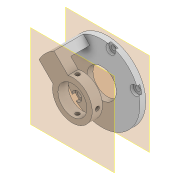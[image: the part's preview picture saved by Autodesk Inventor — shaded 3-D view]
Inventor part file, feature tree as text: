
AUTODESK INVENTOR PART (.ipt)
format: ipt  version: 2022 (Build 260153000, 153)  size: 205,824 bytes
history: native  units: in
note: dims shown in document units (in); Inventor stores cm internally (conversion verified against a paired STEP export)
features: sketch x5, reference x5, extrude x4, other x4, plane x2, hole x1, pattern_circular x1, projected_geometry x1
ambient origin geometry x8: Origin, YZ Plane, XZ Plane, XY Plane, X Axis, Y Axis, Z Axis, Center Point
bodies: Solid1 (feature_tree)
feature tree (23):
  plane  "Work Plane1"
  extrude  "Extrusion1"  Depth=0.7874in
  hole  "Bohrung1"  [1 undecoded]
  plane  "Arbeitsebene3"
  extrude  "Extrusion13"  TaperAngle=135.0deg  [1 undecoded]
  extrude  "Extrusion14"  Depth=0.3937in
  extrude  "Extrusion15"  Depth=0.3937in
  pattern_circular  "Runde Anordnung1"  [2 undecoded]
  sketch  "Sketch1"  dims[d0=0.1575in d1=0.0in]
  reference  "Reference1"
  reference  "Reference5"
  reference  "Reference6"
  reference  "Reference7"
  sketch  "Skizze4"  dims[d9=0.126in d10=0.75in d11=0.2559in d12=0.0787in d13=0.5635in d14=1.0in d15=0.8108in d17=0.7874in]
  reference  "Referenz9"
  sketch  "Skizze19"  dims[d64=0.7874in d65=0.7756in]
  sketch  "Skizze20"  dims[d66=1.063in d67=135.0deg]
  sketch  "Skizze21"  dims[d68=135.0deg d69=0.1181in d70=0.1181in d71=0.2756in d72=0.0in d73=0.2362in d74=0.2756in d75=0.0in d76=0.1102in d77=0.3937in d78=0.0in d79=1.1811in d80=180.0deg]
  projected_geometry  "Projizierte Kontur11"
  other  "<userpath>\Documents\Matchboxscope\INVENTOR\Matchboxscope_v1.iam"
  other  "Matchboxscope_v1.iam"
  other  "Matchboxscope_middle2_v1:1"
  other  "Matchboxscope_middle2_v2:1"
note: 4 required parameter values undecoded (feature->parameter linkage not recoverable at this tier; creation-order binding heuristic only, values carry confidence <= 0.55)
